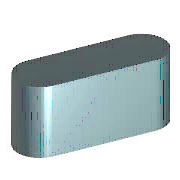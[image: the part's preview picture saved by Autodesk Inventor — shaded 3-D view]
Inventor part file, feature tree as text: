
AUTODESK INVENTOR PART (.ipt)
format: ipt  version: 2025 (Build 290162000, 162)  size: 123,392 bytes
history: native  units: mm (DEFAULTED — no unit token found)
features: plane x3, extrude x1
ambient origin geometry x8: Origin, YZ Plane, XZ Plane, XY Plane, X Axis, Y Axis, Z Axis, Center Point
bodies: Solid1 (feature_tree)
feature tree (4):
  plane  "Work Plane1"
  plane  "Work Plane2"
  extrude  "轴承体1"  Depth=9.0mm
  plane  "Work Plane3"
